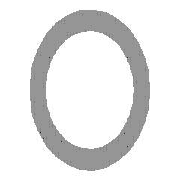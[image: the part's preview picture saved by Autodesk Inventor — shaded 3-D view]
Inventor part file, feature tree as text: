
AUTODESK INVENTOR PART (.ipt)
format: ipt  version: 2021 (Build 250183000, 183)  size: 230,912 bytes
history: native  units: mm (DEFAULTED — no unit token found)
features: other x5, plane x2, sketch x2, sweep x1
ambient origin geometry x8: Origin, YZ Plane, XZ Plane, XY Plane, X Axis, Y Axis, Z Axis, Center Point
bodies: Solid1 (feature_tree)
feature tree (10):
  parser-record x1  (decoder bookkeeping rows leaked as tree rows — omitted from the tree; the rows remain in map.json)
  other  "Driven Length"
  other  "Plano inicial"
  other  "Plano final"
  other  "Trayectoria de barrido"
  plane  "Plano de trabajo de orientación"
  sweep  "Cuerpo"
  sketch  "Sketch3"  dims[d0=33.528mm d1=4.5466mm]
  plane  "Work Plane3"
  sketch  "Sketch4"  dims[d4=-0.0mm d5=734.209592mm d6=90.0deg d7=734.209592mm d8=0.0mm d9=0.0mm]
